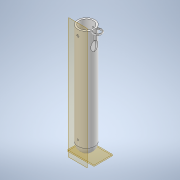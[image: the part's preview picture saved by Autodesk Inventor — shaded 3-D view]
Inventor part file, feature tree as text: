
AUTODESK INVENTOR PART (.ipt)
format: ipt  version: 2022.3 (Build 263350000, 350)  size: 350,208 bytes
history: native  units: mm
features: extrude x17, sketch x13, hole x4, projected_geometry x3, plane x2, fillet x2, revolve x1, mirror x1, sweep x1, thicken_offset x1
ambient origin geometry x8: Origin, YZ Plane, XZ Plane, XY Plane, X Axis, Y Axis, Z Axis, Center Point
bodies: Solid1 (feature_tree)
feature tree (45):
  extrude  "Extrusion1"  Depth=3.0mm
  revolve  "Revolution1"  [1 undecoded]
  sketch  "Sketch3"  dims[d2=180.0mm d3=0.0mm d4=15.0mm]
  extrude  "Extrusion3"  TaperAngle=90.0deg  [1 undecoded]
  extrude  "Extrusion4"  Depth=10.0mm
  extrude  "Extrusion5"  Depth=20.0mm TaperAngle=0.0deg
  sketch  "Sketch4"  dims[d5=15.0mm d6=90.0deg]
  extrude  "Extrusion6"  Depth=10.0mm TaperAngle=0.0deg
  extrude  "Extrusion7"  Depth=30.0mm TaperAngle=0.0deg
  plane  "Work Plane1"
  hole  "Hole1"  [1 undecoded]
  mirror  "Mirror1"
  extrude  "Extrusion8"  Depth=10.0mm
  sketch  "Sketch7"  dims[d12=200.0mm d13=0.0mm d14=10.0mm d15=0.0mm]
  extrude  "Extrusion9"  Depth=6.0mm TaperAngle=0.0deg
  extrude  "Extrusion10"  Depth=6.0mm
  hole  "Hole2"  [1 undecoded]
  sweep  "Sweep1"
  sketch  "Sketch12"  dims[d23=15.0mm d24=10.0mm]
  extrude  "Extrusion11"  TaperAngle=0.0deg  [1 undecoded]
  fillet  "Fillet1"  Radius=15.0mm
  thicken_offset  "Thicken1"
  extrude  "Extrusion2"  Depth=1.0mm
  hole  "Hole7"  [1 undecoded]
  sketch  "Sketch20"  dims[d34=22.0mm d35=6.0mm]
  extrude  "Extrusion14"  Depth=1.0mm
  extrude  "Extrusion15"  Depth=1.0mm
  plane  "Work Plane6"
  hole  "Hole8"  [1 undecoded]
  sketch  "Sketch22"  dims[d40=7.5mm d41=15.0mm d42=0.0mm d43=2.2mm d44=6.0mm d45=3.1mm d46=4.1mm d47=90.0deg d48=0.9mm d49=0.0mm d52=15.0mm d53=1.0mm d54=12.0mm d55=20.0mm d56=15.0mm d57=20.0mm d58=2.0mm d59=0.0mm d60=0.0mm d61=2.0mm d62=160.0mm d63=0.0mm d64=1.0mm d83=20.0mm d84=20.0mm d85=10.0mm d86=0.0mm d107=3.4mm d108=6.0mm d109=4.1mm d110=5.1mm d111=90.0deg d112=15.0mm d113=0.0mm d114=6.2mm d115=0.0mm d116=0.0mm d117=8.0mm d118=12.0mm d119=0.0mm d120=-10.0mm d121=3.4mm d122=6.0mm d123=4.1mm d124=5.1mm d125=90.0deg d126=3.9mm d127=0.0mm d128=8.0mm d129=6.2mm d130=0.0mm d131=0.0mm d132=3.0mm d133=0.0mm d134=80.0mm d135=15.0mm d136=20.0mm d137=158.0mm d138=0.0mm d139=2.0mm d140=0.0mm d141=1.0mm d142=5.0mm d143=20.0mm d144=2.0mm d50=0.75mm d51=20.594885mm d105=0.5mm d106=0.872665mm]
  extrude  "Extrusion16"  Depth=1.0mm
  extrude  "Extrusion17"  TaperAngle=0.0deg  [1 undecoded]
  extrude  "Extrusion18"  Depth=1.0mm
  extrude  "Extrusion19"  Depth=1.0mm TaperAngle=0.0deg
  fillet  "Fillet2"  Radius=1.0mm
  sketch  "Sketch1"  dims[d0=30.0mm d1=3.0mm]
  sketch  "Sketch5"  dims[d7=10.0mm d8=3.0mm]
  sketch  "Sketch6"  dims[d9=5.2mm d10=20.0mm d11=0.0mm]
  projected_geometry  "Projected Loop1"
  sketch  "Sketch8"  dims[d16=5.075mm d17=0.0mm d18=30.0mm d19=0.0mm]
  sketch  "Sketch10"  dims[d20=25.0mm d21=0.0mm d22=0.1mm]
  projected_geometry  "Projected Loop2"
  sketch  "Sketch19"  dims[d25=2.2mm d26=6.0mm d27=4.0mm d28=2.0mm d29=90.0deg d30=5.0mm d31=0.0mm d32=155.0mm d33=0.0mm]
  sketch  "Sketch21"  dims[d36=51.0mm d37=0.0mm d38=30.0mm d39=0.0mm]
  projected_geometry  "Projected Loop4"
note: 8 required parameter values undecoded (feature->parameter linkage not recoverable at this tier; creation-order binding heuristic only, values carry confidence <= 0.55)